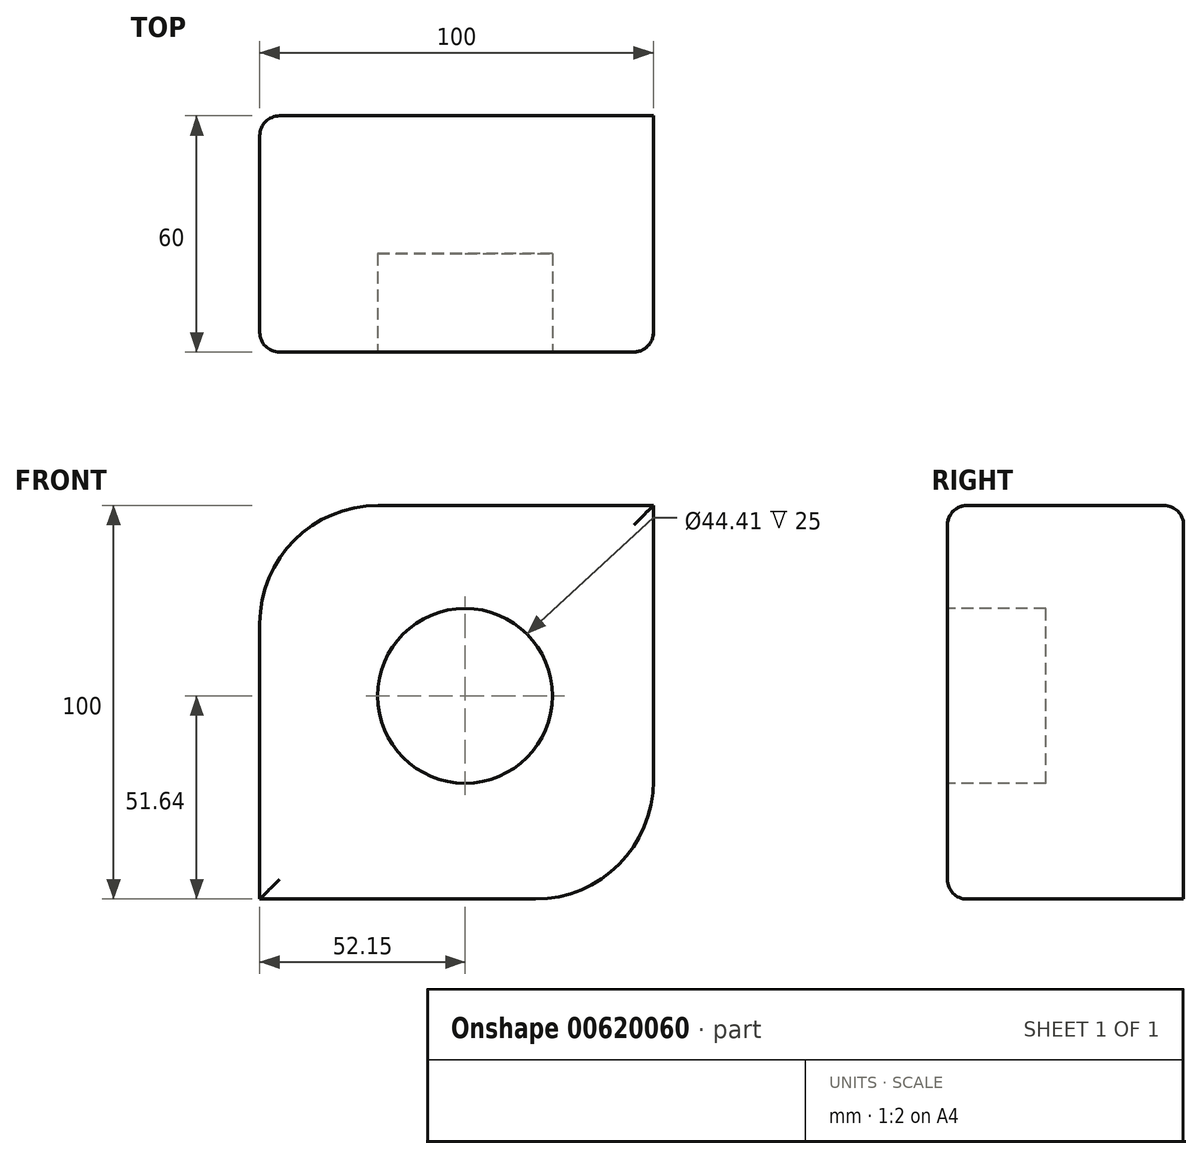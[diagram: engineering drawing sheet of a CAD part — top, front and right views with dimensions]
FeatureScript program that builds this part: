
annotation { "Feature Type Name" : "Feature", "Feature Type Description" : "" }
export const myFeature = defineFeature(function(context is Context, id is Id, definition is map)
    precondition{}
    {
        {
            var Q0;
            Q0=qCreatedBy(makeId("Front.planeOp"),FACE);
            var sketch = newSketch(context, id + "F0", { "sketchPlane" : qUnion([Q0])});
            skLineSegment(sketch, "E0.bottom", {"start": v(-22.15, 75.71) * mm, "end": v(47.85, 75.71) * mm});
            skLineSegment(sketch, "E0.top", {"start": v(-52.15, -24.29) * mm, "end": v(17.85, -24.29) * mm});
            skLineSegment(sketch, "E0.left", {"start": v(-52.15, 45.71) * mm, "end": v(-52.15, -24.29) * mm});
            skLineSegment(sketch, "E0.right", {"start": v(47.85, 75.71) * mm, "end": v(47.85, 5.71) * mm});
            skPoint(sketch, "E1.visualSharp", {"position": v(-52.15, 75.71) * mm});
            skArc(sketch, "E1.filletArc", {"start": v(-22.15, 75.71) * mm, "mid": v(-43.36, 66.93) * mm, "end": v(-52.15, 45.71) * mm});
            skPoint(sketch, "E2.visualSharp", {"position": v(47.85, -24.29) * mm});
            skArc(sketch, "E2.filletArc", {"start": v(17.85, -24.29) * mm, "mid": v(39.07, -15.5) * mm, "end": v(47.85, 5.71) * mm});
            skSolve(sketch);
        }
        {
            var Q0;
            Q0=makeQuery(id+"F0.imprint","IMPRINT",FACE,{"disambiguationData":[TD([[makeQuery(id+"F0.imprint","IMPRINT",EDGE,{"derivedFrom":sQuery(id+"F0.wireOp",EDGE,"E0.bottom")}),-1.0]])]});
            extrude(context, id + "F1", {"entities" : qUnion([Q0]), "depth" : 60 * mm, "offsetDistance" : 25 * mm});
        }
        {
            var Q0;
            Q0=makeQuery(id+"F1.opExtrude","SWEPT_FACE",FACE,{"disambiguationData":[OSD([sQuery(id+"F0.wireOp",EDGE,"E1.filletArc")])]});
            var Q1;
            Q1=makeQuery(id+"F1.opExtrude","CAP_FACE",FACE,{"disambiguationData":[OSD([sQuery(id+"F0.wireOp",EDGE,"E0.bottom"),sQuery(id+"F0.wireOp",EDGE,"E0.top"),sQuery(id+"F0.wireOp",EDGE,"E0.left"),sQuery(id+"F0.wireOp",EDGE,"E0.right"),sQuery(id+"F0.wireOp",EDGE,"E1.filletArc"),sQuery(id+"F0.wireOp",EDGE,"E2.filletArc")])],"isStart":false});
            fillet(context, id + "F2", {"entities" : qUnion([Q0, Q1]), "radius" : 5 * mm, "tangentPropagation" : true, "allowEdgeOverflow" : false});
        }
        {
            var Q0;
            Q0=makeQuery(id+"F1.opExtrude","CAP_FACE",FACE,{"disambiguationData":[OSD([sQuery(id+"F0.wireOp",EDGE,"E0.bottom"),sQuery(id+"F0.wireOp",EDGE,"E0.top"),sQuery(id+"F0.wireOp",EDGE,"E0.left"),sQuery(id+"F0.wireOp",EDGE,"E0.right"),sQuery(id+"F0.wireOp",EDGE,"E1.filletArc"),sQuery(id+"F0.wireOp",EDGE,"E2.filletArc")])],"isStart":false});
            var sketch = newSketch(context, id + "F3", { "sketchPlane" : qUnion([Q0])});
            skCircle(sketch, "E3", {"center": v(0, 27.35) * mm, "radius": 22.2 * mm});
            skSolve(sketch);
        }
        {
            var Q0;
            Q0 = qSketchRegion(id + "F3", true);
            extrude(context, id + "F4", {"entities" : qUnion([Q0]), "operationType" : NewBodyOperationType.REMOVE, "oppositeDirection" : true, "depth" : 25 * mm, "offsetDistance" : 25 * mm});
        }
    });
